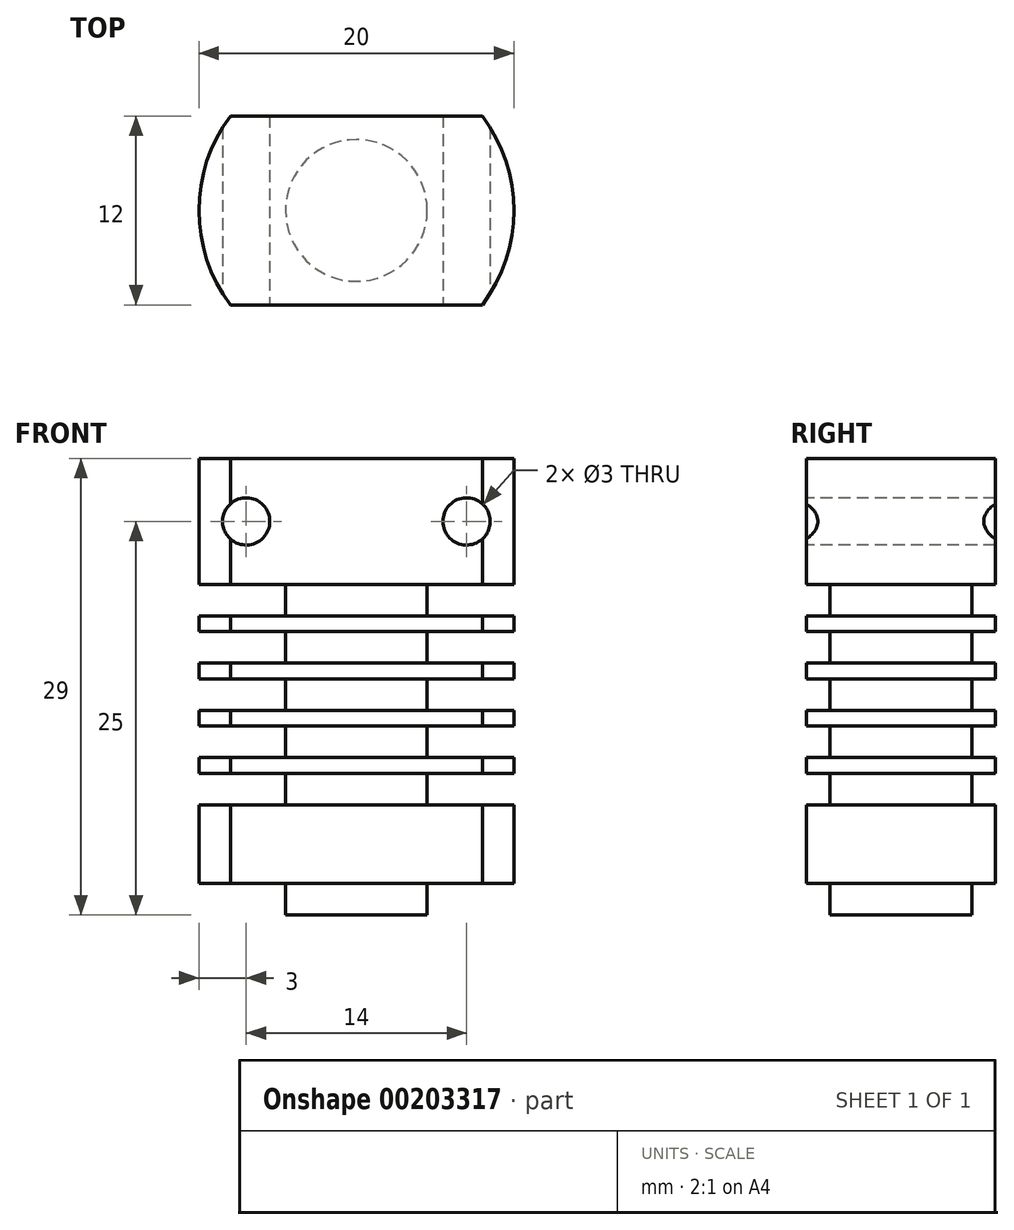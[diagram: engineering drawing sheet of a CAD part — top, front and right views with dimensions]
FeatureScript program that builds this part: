
annotation { "Feature Type Name" : "Feature", "Feature Type Description" : "" }
export const myFeature = defineFeature(function(context is Context, id is Id, definition is map)
    precondition{}
    {
        {
            var Q0;
            Q0=qCreatedBy(makeId("Top.planeOp"),FACE);
            var sketch = newSketch(context, id + "F0", { "sketchPlane" : qUnion([Q0])});
            skLineSegment(sketch, "E0.bottom", {"start": v(8, -6) * mm, "end": v(-8, -6) * mm});
            skLineSegment(sketch, "E0.top", {"start": v(8, 6) * mm, "end": v(-8, 6) * mm});
            skPoint(sketch, "E0.middle", {"position": v(0, 0) * mm});
            skArc(sketch, "E1", {"start": v(-8, 6) * mm, "mid": v(-10, 0) * mm, "end": v(-8, -6) * mm});
            skArc(sketch, "E2.trimOffspring", {"start": v(8, -6) * mm, "mid": v(10, 0) * mm, "end": v(8, 6) * mm});
            skPoint(sketch, "E3.orphan", {"position": v(-10, -6) * mm});
            skPoint(sketch, "E4.orphan", {"position": v(-10, 6) * mm});
            skPoint(sketch, "E5.orphan", {"position": v(10, 6) * mm});
            skPoint(sketch, "E6.orphan", {"position": v(10, -6) * mm});
            skSolve(sketch);
        }
        {
            var Q0;
            Q0=makeQuery(id+"F0.imprint","IMPRINT",FACE,{"disambiguationData":[TD([[makeQuery(id+"F0.imprint","IMPRINT",EDGE,{"derivedFrom":sQuery(id+"F0.wireOp",EDGE,"E0.bottom")}),-1.0]])]});
            extrude(context, id + "F1", {"entities" : qUnion([Q0]), "depth" : 27 * mm});
        }
        {
            var Q0;
            Q0=qCreatedBy(makeId("Front.planeOp"),FACE);
            var sketch = newSketch(context, id + "F2", { "sketchPlane" : qUnion([Q0])});
            skLineSegment(sketch, "E7.bottom", {"start": v(15, 5) * mm, "end": v(-15, 5) * mm});
            skLineSegment(sketch, "E7.top", {"start": v(15, 7) * mm, "end": v(-15, 7) * mm});
            skLineSegment(sketch, "E7.left", {"start": v(15, 5) * mm, "end": v(15, 7) * mm});
            skLineSegment(sketch, "E7.right", {"start": v(-15, 5) * mm, "end": v(-15, 7) * mm});
            skPoint(sketch, "E7.middle", {"position": v(0, 6) * mm});
            skLineSegment(sketch, "E8.0.1.0", {"start": v(15, 10) * mm, "end": v(-15, 10) * mm});
            skLineSegment(sketch, "E8.0.1.1", {"start": v(15, 8) * mm, "end": v(-15, 8) * mm});
            skPoint(sketch, "E8.0.1.2", {"position": v(0, 9) * mm});
            skLineSegment(sketch, "E8.0.1.3", {"start": v(-15, 8) * mm, "end": v(-15, 10) * mm});
            skLineSegment(sketch, "E8.0.1.4", {"start": v(15, 8) * mm, "end": v(15, 10) * mm});
            skLineSegment(sketch, "E8.0.2.0", {"start": v(15, 13) * mm, "end": v(-15, 13) * mm});
            skLineSegment(sketch, "E8.0.2.1", {"start": v(15, 11) * mm, "end": v(-15, 11) * mm});
            skPoint(sketch, "E8.0.2.2", {"position": v(0, 12) * mm});
            skLineSegment(sketch, "E8.0.2.3", {"start": v(-15, 11) * mm, "end": v(-15, 13) * mm});
            skLineSegment(sketch, "E8.0.2.4", {"start": v(15, 11) * mm, "end": v(15, 13) * mm});
            skLineSegment(sketch, "E8.0.3.0", {"start": v(15, 16) * mm, "end": v(-15, 16) * mm});
            skLineSegment(sketch, "E8.0.3.1", {"start": v(15, 14) * mm, "end": v(-15, 14) * mm});
            skPoint(sketch, "E8.0.3.2", {"position": v(0, 15) * mm});
            skLineSegment(sketch, "E8.0.3.3", {"start": v(-15, 14) * mm, "end": v(-15, 16) * mm});
            skLineSegment(sketch, "E8.0.3.4", {"start": v(15, 14) * mm, "end": v(15, 16) * mm});
            skLineSegment(sketch, "E8.0.4.0", {"start": v(15, 19) * mm, "end": v(-15, 19) * mm});
            skLineSegment(sketch, "E8.0.4.1", {"start": v(15, 17) * mm, "end": v(-15, 17) * mm});
            skPoint(sketch, "E8.0.4.2", {"position": v(0, 18) * mm});
            skLineSegment(sketch, "E8.0.4.3", {"start": v(-15, 17) * mm, "end": v(-15, 19) * mm});
            skLineSegment(sketch, "E8.0.4.4", {"start": v(15, 17) * mm, "end": v(15, 19) * mm});
            skLineSegment(sketch, "E8.direction1", {"start": v(-15, 5) * mm, "end": v(10, 5) * mm, "construction": true});
            skLineSegment(sketch, "E8.direction2", {"start": v(-15, 5) * mm, "end": v(-15, 8) * mm, "construction": true});
            skSolve(sketch);
        }
        {
            var Q0;
            Q0 = qSketchRegion(id + "F2", true);
            extrude(context, id + "F3", {"entities" : qUnion([Q0]), "operationType" : NewBodyOperationType.REMOVE, "endBound" : BoundingType.SYMMETRIC, "oppositeDirection" : true, "depth" : 12 * mm});
        }
        {
            var Q0;
            Q0=qCreatedBy(makeId("Top.planeOp"),FACE);
            var sketch = newSketch(context, id + "F4", { "sketchPlane" : qUnion([Q0])});
            skCircle(sketch, "E9", {"center": v(0, 0) * mm, "radius": 4.5 * mm});
            skSolve(sketch);
        }
        {
            var Q0;
            Q0=makeQuery(id+"F4.imprint","IMPRINT",FACE,{"disambiguationData":[TD([[makeQuery(id+"F4.imprint","IMPRINT",EDGE,{"derivedFrom":sQuery(id+"F4.wireOp",EDGE,"E9")}),1.0]])]});
            var Q1;
            Q1=sQuery(id+"F4.wireOp",EDGE,"E9");
            extrude(context, id + "F5", {"entities" : qUnion([Q0]), "operationType" : NewBodyOperationType.ADD, "surfaceEntities" : qUnion([Q1]), "depth" : 27 * mm, "hasSecondDirection" : true, "secondDirectionOppositeDirection" : true, "secondDirectionDepth" : 2 * mm});
        }
        {
            var Q0;
            Q0=qCreatedBy(makeId("Front.planeOp"),FACE);
            var sketch = newSketch(context, id + "F6", { "sketchPlane" : qUnion([Q0])});
            skCircle(sketch, "E10", {"center": v(-7, 23) * mm, "radius": 1.5 * mm});
            skCircle(sketch, "E11.MirrorC", {"center": v(7, 23) * mm, "radius": 1.5 * mm});
            skSolve(sketch);
        }
        {
            var Q0;
            Q0 = qSketchRegion(id + "F6", true);
            extrude(context, id + "F7", {"entities" : qUnion([Q0]), "operationType" : NewBodyOperationType.REMOVE, "endBound" : BoundingType.SYMMETRIC, "oppositeDirection" : true, "depth" : 12 * mm});
        }
    });
